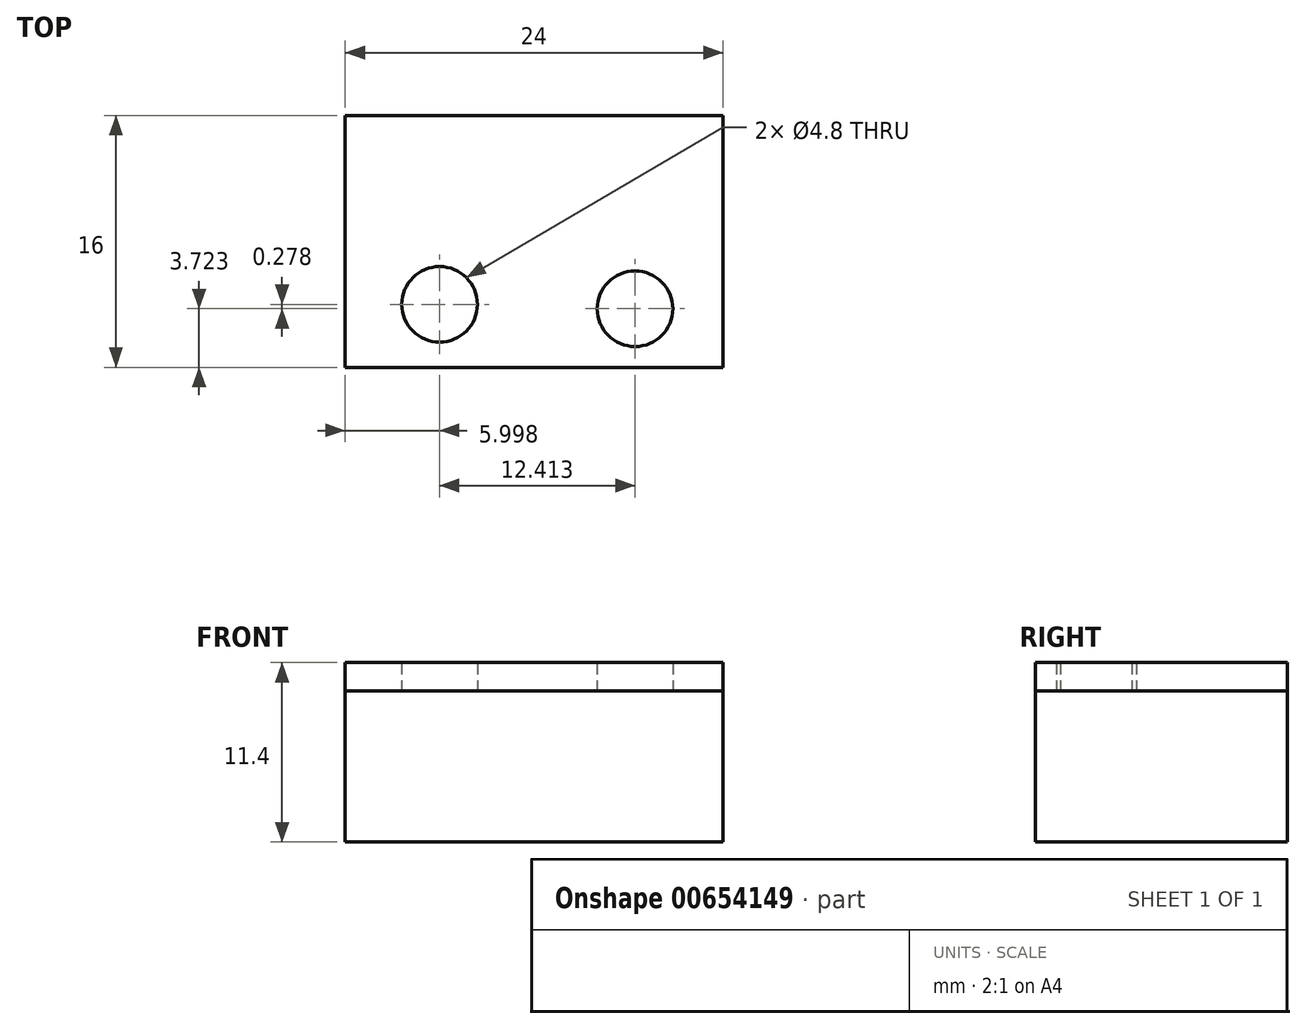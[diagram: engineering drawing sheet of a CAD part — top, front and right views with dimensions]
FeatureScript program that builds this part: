
annotation { "Feature Type Name" : "Feature", "Feature Type Description" : "" }
export const myFeature = defineFeature(function(context is Context, id is Id, definition is map)
    precondition{}
    {
        {
            var Q0;
            Q0=qCreatedBy(makeId("Top.planeOp"),FACE);
            var sketch = newSketch(context, id + "F0", { "sketchPlane" : qUnion([Q0])});
            skLineSegment(sketch, "E0.bottom", {"start": v(0, 0) * mm, "end": v(-24, 0) * mm});
            skLineSegment(sketch, "E0.top", {"start": v(0, 16) * mm, "end": v(-24, 16) * mm});
            skLineSegment(sketch, "E0.left", {"start": v(0, 0) * mm, "end": v(0, 16) * mm});
            skLineSegment(sketch, "E0.right", {"start": v(-24, 0) * mm, "end": v(-24, 16) * mm});
            skSolve(sketch);
        }
        {
            var Q0;
            Q0=makeQuery(id+"F0.imprint","IMPRINT",FACE,{"disambiguationData":[TD([[makeQuery(id+"F0.imprint","IMPRINT",EDGE,{"derivedFrom":sQuery(id+"F0.wireOp",EDGE,"E0.bottom")}),-1.0]])]});
            extrude(context, id + "F1", {"entities" : qUnion([Q0]), "depth" : 9.6 * mm, "offsetDistance" : 25.4 * mm});
        }
        {
            var Q0;
            Q0=makeQuery(id+"F1.opExtrude","CAP_FACE",FACE,{"disambiguationData":[OSD([sQuery(id+"F0.wireOp",EDGE,"E0.bottom"),sQuery(id+"F0.wireOp",EDGE,"E0.top"),sQuery(id+"F0.wireOp",EDGE,"E0.left"),sQuery(id+"F0.wireOp",EDGE,"E0.right")])],"isStart":false});
            var sketch = newSketch(context, id + "F2", { "sketchPlane" : qUnion([Q0])});
            skLineSegment(sketch, "E1", {"start": v(-24, 8) * mm, "end": v(0, 8) * mm, "construction": true});
            skLineSegment(sketch, "E2", {"start": v(-12, 16) * mm, "end": v(-12, 0) * mm, "construction": true});
            skLineSegment(sketch, "E3", {"start": v(-24, 16) * mm, "end": v(-12, 8) * mm, "construction": true});
            skLineSegment(sketch, "E4", {"start": v(-12, 8) * mm, "end": v(0, 16) * mm, "construction": true});
            skCircle(sketch, "E5", {"center": v(-18, 12) * mm, "radius": 2.4 * mm});
            skCircle(sketch, "E6", {"center": v(-5.59, 12.28) * mm, "radius": 2.4 * mm});
            skCircle(sketch, "E7.MirrorC", {"center": v(-18, 4) * mm, "radius": 2.4 * mm});
            skCircle(sketch, "E8.MirrorC", {"center": v(-5.59, 3.72) * mm, "radius": 2.4 * mm, "construction": true});
            skCircle(sketch, "E9.MirrorC", {"center": v(-18, 4) * mm, "radius": 2.4 * mm, "construction": true});
            skCircle(sketch, "E10.MirrorC", {"center": v(-5.59, 3.72) * mm, "radius": 2.4 * mm});
            skSolve(sketch);
        }
        {
            var Q0;
            Q0=makeQuery(id+"F2.imprint","IMPRINT",FACE,{"disambiguationData":[TD([[makeQuery(id+"F2.imprint","IMPRINT",EDGE,{"derivedFrom":sQuery(id+"F2.wireOp",EDGE,"E5")}),1.0]])]});
            var Q1;
            Q1=makeQuery(id+"F2.imprint","IMPRINT",FACE,{"disambiguationData":[TD([[makeQuery(id+"F2.imprint","IMPRINT",EDGE,{"derivedFrom":sQuery(id+"F2.wireOp",EDGE,"E6")}),1.0]])]});
            var Q2;
            Q2=makeQuery(id+"F2.imprint","IMPRINT",FACE,{"disambiguationData":[TD([[makeQuery(id+"F2.imprint","IMPRINT",EDGE,{"derivedFrom":sQuery(id+"F2.wireOp",EDGE,"E7.MirrorC")}),-1.0]])]});
            var Q3;
            Q3=makeQuery(id+"F2.imprint","IMPRINT",FACE,{"disambiguationData":[TD([[makeQuery(id+"F2.imprint","IMPRINT",EDGE,{"derivedFrom":sQuery(id+"F2.wireOp",EDGE,"E10.MirrorC")}),-1.0]])]});
            extrude(context, id + "F3", {"entities" : qUnion([Q0, Q1, Q2, Q3]), "depth" : 1.8 * mm, "offsetDistance" : 25.4 * mm});
        }
    });
